# Revit family: Trim_Kit_Shower-GROHE-Concetto-35073_Series - Copy
name_source: partatom
category: Plumbing Fixtures
revit_build: Autodesk Revit 2014 (Build: 20130308_1515(x64)
units: mm (PartAtom-declared; Revit-internal decimal feet)

## types (3) — shared parameters
ADA Compliant = No
Assembly Code = D2010710
CW Connection = Yes
CWFU = 1.5
Cold Water Connection Diameter = 1/2"
Cold Water Connection Radius = 1/4"
Default Elevation = 40"
Description = Concetto Bathtub/Shower Combo Faucet
Flow Rate = 2.0 gpm
HW Connection = Yes
HWFU = 1.5
Height = 40"
Hot Water Connection Diameter = 1"
Hot Water Connection Radius = 1/4"
Installation Type = Wall Mounted
Length = 2 15/16"
Manufacturer = Grohe
Price = Prices may vary. Please consult Manufacturer Representative for most up-to-date price list.
Product Page URL = https://www.grohe.ca
Tempered Connection Diameter = 1/2"
Tempered Connection Radius = 1/4"
URL = https://www.grohe.com
Vent Connection = No
WFU = 2
Warranty Documentation Link = https://cdn.cloud.grohe.com
Waste Connection = No
Width = 6 11/16"

## per-type parameters (varying)
| type | Finish | Material |
| 3507310A | Metal-Grohe-001-Chrome | Metal-Grohe-001-Chrome |
| 35073EN1 | Metal-Grohe-EN1-Brushed Nickel | Metal-Grohe-EN1-Brushed Nickel |
| 35073ENA | Metal-Grohe-EN1-Brushed Nickel | Metal-Grohe-EN1-Brushed Nickel |

note: column(s) folded — value = type name in every type: Model

## geometry (parser evidence)
native form markers: Sweep x4
no freeform markers — native parametric forms only
